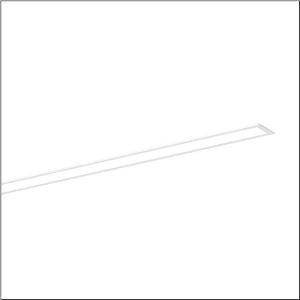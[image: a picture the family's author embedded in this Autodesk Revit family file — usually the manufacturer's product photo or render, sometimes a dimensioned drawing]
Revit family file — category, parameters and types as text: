
# Revit family: silica_r__21_51mx10tat2w_99a0
name_source: partatom
category: Lighting Fixtures
units: mm (PartAtom-declared; Revit-internal decimal feet)

## family parameters
Cut with Voids When Loaded = No
Host = Face
Light Source = No
Part Type = Normal
Room Calculation Point = No
Round Connector Dimension = Use Diameter
Shared = No

## types (1)
- --- (1 x LED, 2400 lm, 20.5 W, 6500K)
    Apparent Load = 21 VA
    CIE Flux Codes = 48 79 96 100 100
    Color Rendering = 80
    Color Temperature = 6500K
    Default Elevation = 1800 mm
    Description = Silica® 21, office luminaire, primary optical cover: cover, of PMMA, opal, light emission: direct distribution, primary light characteristic: symmetric, installation type: recessed, LED, rated luminous flux: 2.400lm, luminous efficacy: 112lm/W, light colour: 8tw, colour temperature: 2700..6500K, with terminal, 3+2-pole, max. 2.5mm², mains connection: 220..240V, AC, 50/60Hz, rated input power: 21.5W, luminaire housing, of aluminium, traffic white (RAL 9016), length: 1.228mm, width: 79mm, height: 53mm, protection rating (complete): IP20, insulation class (complete): insulation class I (protective earthing), certification: CE, permissible operating ambient temperature: 0..+35°C, standard: EN 50419, packaging unit: 1 piece
    Height = 0 mm  [stored 0 ft]
    Lamp = 1 x LED
    Lamp Light Flux = 2400 lm
    Lamp Power = 20.5 W
    Lamp count = 1
    Length = 1227 mm
    Luminous efficacy = 117 lm/W
    Manufacturer = Siteco
    ModVariant = No
    Model = 51MX10TAT2W
    Mounting Place = Ceiling
    Mounting Type = Recessed
    Number of Poles = 1
    OnlyDefault = Yes
    Power Factor = 1
    Product Name = Silica® 21
    Product group = office luminaire | ceiling recessed
    ProductGroupID = 401
    Protection Class = Protection class I
    Protection Degree = IP 20
    RLX_Detail_Level = 1
    RLX_Emergency_Light_Flux = 0 lm
    RLX_Emergency_Type = 0
    RLX_Emergency_Type_DB = No
    RlxData = <blob elided: 17869 chars, md5=e5d53678>
    Socket = socket
    Standby Power = 0 W
    System Light Flux = 2400 lm
    System Power = 21 W
    Type Comments = individual setting
    Type Image = l_1297737.jpg
    URL = http://relux.com
    VarID = @adj_071053
    Voltage = 0 V
    Weight = 0.00 kg
    Width = 79 mm

note: [stored X ft] marks values corroborated as IEEE doubles in the binary element streams (Revit-internal decimal feet)

## geometry (parser evidence)
native form markers: Blend x4, Sweep x11
no freeform markers — native parametric forms only
